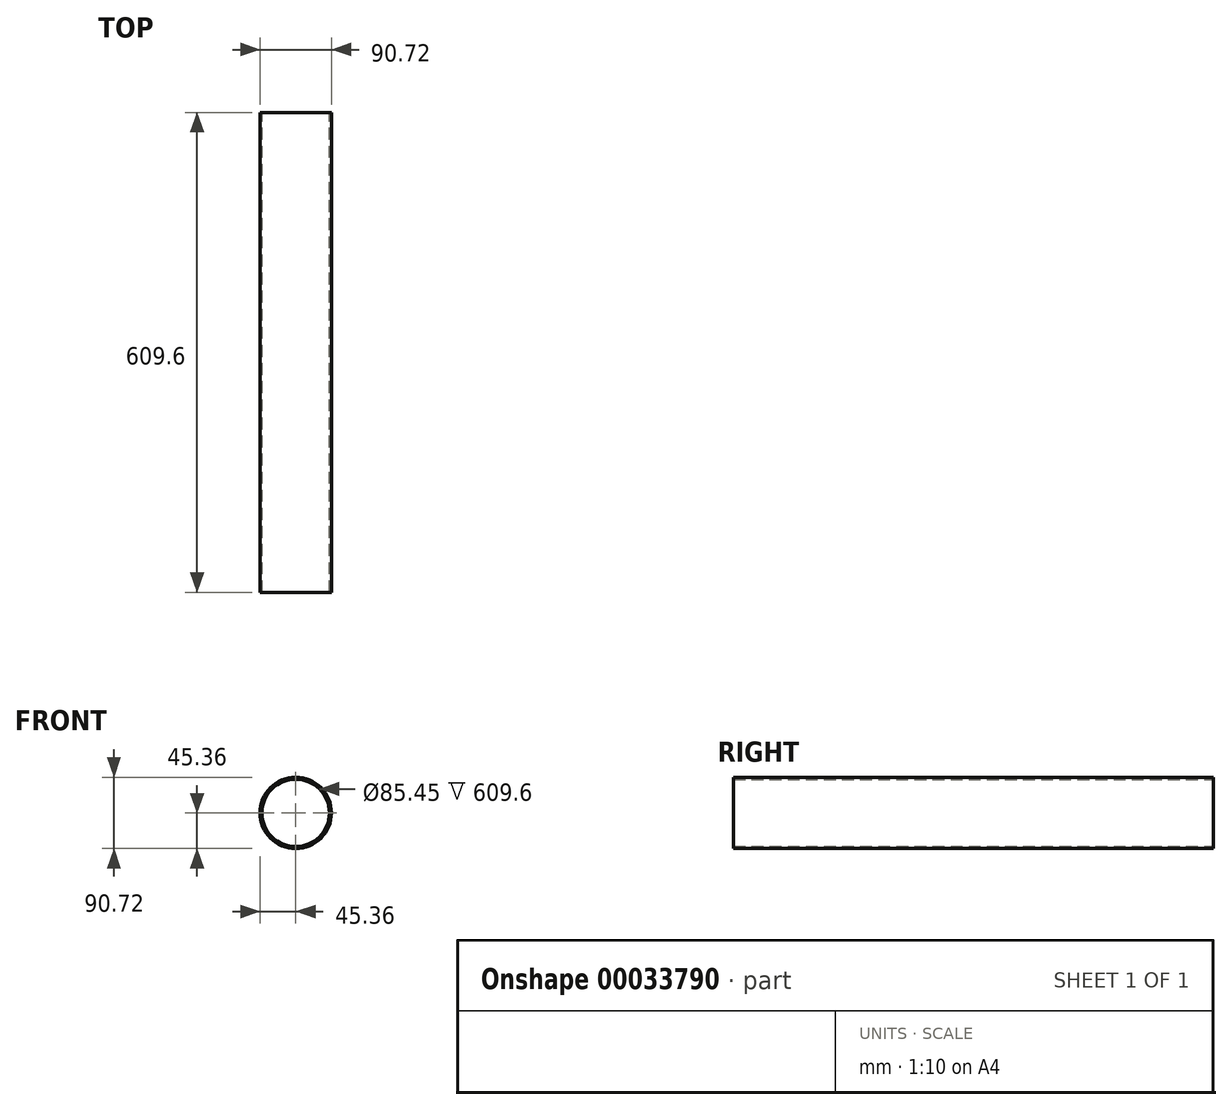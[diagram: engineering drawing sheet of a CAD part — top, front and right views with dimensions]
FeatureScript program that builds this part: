
annotation { "Feature Type Name" : "Feature", "Feature Type Description" : "" }
export const myFeature = defineFeature(function(context is Context, id is Id, definition is map)
    precondition{}
    {
        {
            var Q0;
            Q0=qCreatedBy(makeId("Front.planeOp"),FACE);
            var sketch = newSketch(context, id + "F0", { "sketchPlane" : qUnion([Q0])});
            skCircle(sketch, "E0", {"center": v(0, 0) * mm, "radius": 45.36 * mm});
            skCircle(sketch, "E1", {"center": v(0, 0) * mm, "radius": 42.73 * mm});
            skSolve(sketch);
        }
        {
            var Q0;
            Q0=makeQuery(id+"F0.imprint","IMPRINT",FACE,{"disambiguationData":[TD([[makeQuery(id+"F0.imprint","IMPRINT",EDGE,{"derivedFrom":sQuery(id+"F0.wireOp",EDGE,"E0")}),1.0]])]});
            var Q1;
            Q1=sQuery(id+"F0.wireOp",EDGE,"E0");
            extrude(context, id + "F1", {"entities" : qUnion([Q0]), "surfaceEntities" : qUnion([Q1]), "depth" : 609.6 * mm});
        }
    });
